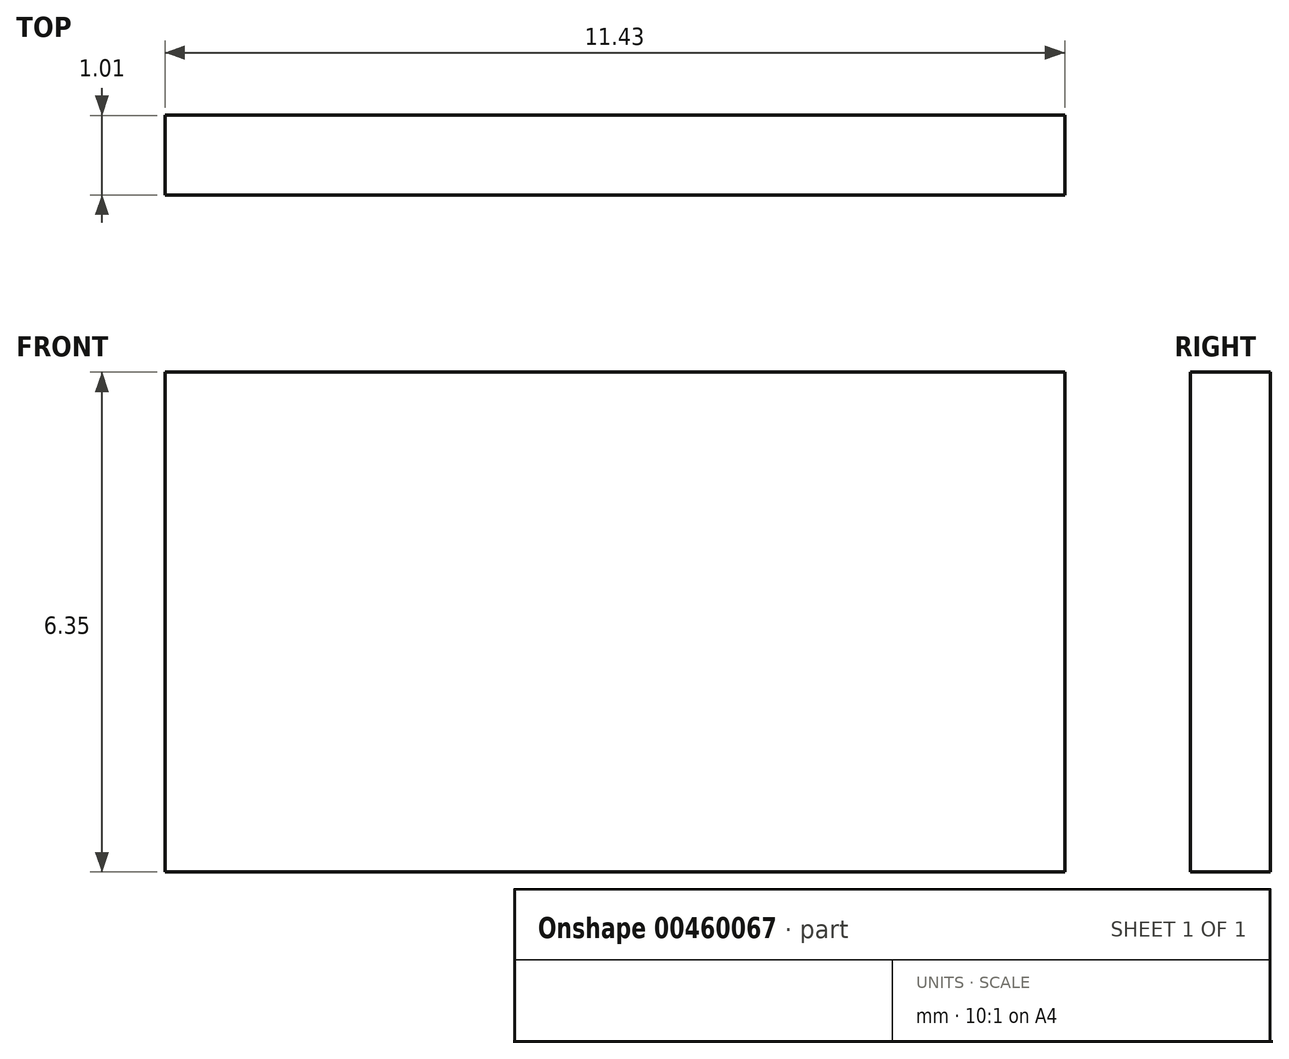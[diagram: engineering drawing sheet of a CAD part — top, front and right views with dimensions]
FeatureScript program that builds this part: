
annotation { "Feature Type Name" : "Feature", "Feature Type Description" : "" }
export const myFeature = defineFeature(function(context is Context, id is Id, definition is map)
    precondition{}
    {
        {
            var Q0;
            Q0=qCreatedBy(makeId("Top.planeOp"),FACE);
            var sketch = newSketch(context, id + "F0", { "sketchPlane" : qUnion([Q0])});
            skLineSegment(sketch, "E0.bottom", {"start": v(0.06, 6.66) * mm, "end": v(11.5, 6.66) * mm});
            skLineSegment(sketch, "E0.top", {"start": v(0.06, 5.65) * mm, "end": v(11.5, 5.65) * mm});
            skLineSegment(sketch, "E0.left", {"start": v(0.06, 6.66) * mm, "end": v(0.06, 5.65) * mm});
            skLineSegment(sketch, "E0.right", {"start": v(11.5, 6.66) * mm, "end": v(11.5, 5.65) * mm});
            skSolve(sketch);
        }
        {
            var Q0;
            Q0 = qSketchRegion(id + "F0", true);
            extrude(context, id + "F1", {"entities" : qUnion([Q0]), "depth" : 6.35 * mm});
        }
    });
